# Revit family: CUW
name_source: partatom
category: Lighting Fixtures
units: mm (PartAtom-declared; Revit-internal decimal feet)

## family parameters
Cut with Voids When Loaded = No
Host = Face
Light Source = Yes
OmniClass Number = 23.80.70.11.21
OmniClass Title = Emergency Lighting
Part Type = Normal
Room Calculation Point = No
Round Connector Dimension = Use Diameter
Shared = No

## types (2) — shared parameters
Apparent Load = 0 VA
Color Filter = 16777215
Default Elevation = 48.000"
Description = Decorative LED AC/Emergency Light
Dimming Lamp Color Temperature Shift = <None>
Emit Shape Visible in Rendering = No
Emit from Circle Diameter = 6.000"
Finish = Dark Bronze
Glass = Glass
Is 120V = Yes
Is 277V = No
Lamp = LED Lamp
Load Classification = Lighting
Manufacturer = Compass Products
Tilt Angle = 90.00°
URL = https://www.currentlighting.com
Voltage = 120 V
Wattage Comments = 9 W - 52.15 W
Watts = 9 W

## per-type parameters (varying)
| type | Photometric Web File |
| CUW-AC | CUW-AC.ies |
| CUW-DC | CUW-DC.ies |

note: column(s) folded — value = type name in every type: Model

## geometry (parser evidence)
native form markers: Blend x9, Sweep x5
no freeform markers — native parametric forms only
